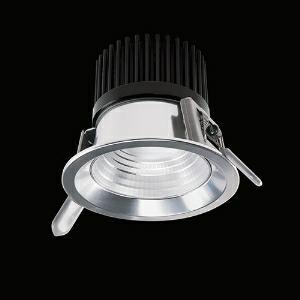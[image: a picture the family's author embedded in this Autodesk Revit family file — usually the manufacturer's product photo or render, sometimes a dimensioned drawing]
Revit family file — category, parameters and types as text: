
# Revit family: spectral_myral_myral_4500-830-s-dali
name_source: partatom
category: Lighting Fixtures
revit_build: Autodesk Revit 2016 (Build: 20150220_1215(x64)
units: mm (PartAtom-declared; Revit-internal decimal feet)

## family parameters
Cut with Voids When Loaded = No
Host = Face
Light Source = No
Part Type = Normal
Room Calculation Point = No
Round Connector Dimension = Use Diameter
Shared = No

## types (1)
- SPECTRAL MYRAL (1 x )
    Apparent Load = 0 VA
    Approval mark = CE
    CIE Flux Codes = 85 100 100 100 100
    Control Gear = Electronic transformer
    Default Elevation = 1800 mm
    Description = SPG0330176
MYRAL recessed spot

Design:
    Height = 0 mm  [stored 0 ft]
    Lamp = 1 x
    Lamp count = 1
    Length = 120 mm
    Luminous efficacy = 0 lm/W
    Manufacturer = Ridi
    ModVariant = No
    Model = MYRAL 4500-830-S-DALI
    Mounting Place = Ceiling
    Mounting Type = Recessed
    Number of Poles = 1
    OnlyDefault = Yes
    Power Factor = 1
    Product Name = SPECTRAL MYRAL
    Product group = Downlight recessed
    ProductGroupID = 400
    Protection Class = Protection class
    Protection Degree = IP 20
    RlxData = <blob elided: 38949 chars, md5=eeba1948>
    Socket = socket
    Standby Power = 0 W
    System Light Flux = 0 lm
    System Power = 0 W
    Type Image = myral_04.jpg
    URL = http://reluxnet.relux.com
    VarID = ---
    Voltage = 0 V
    Weight = 0.00 kg
    Width = 0 mm  [stored 0 ft]

note: [stored X ft] marks values corroborated as IEEE doubles in the binary element streams (Revit-internal decimal feet)

## geometry (parser evidence)
native form markers: Sweep x12
no freeform markers — native parametric forms only
